# Revit family: Flushometer-Toilet_Touchless-KOHLER-Mach_Wave-K-40TD00N10_1
name_source: partatom
category: Plumbing Fixtures
units: mm (PartAtom-declared; Revit-internal decimal feet)

## family parameters
Cut with Voids When Loaded = No
Host = Face
OmniClass Number = 23.27.31.00
OmniClass Title = Valves
Part Type = Normal
Room Calculation Point = No
Round Connector Dimension = Use Diameter
Shared = No

## types (2) — shared parameters
ADA Compliant = Yes
Assembly Code = D2020
CW Connection = Yes
Center Distance = 11 5/8"
Cold Water Inlet = Cold Water Inlet
Cold Water Outlet = Cold Water Outlet
Date Modified = 12/27/2022
Default Elevation = 15"
Finish = Kohler-Metal-CP-Polished_Chrome
Flow Rate = 25 GPM
Flush Rate- GPF = 1.28 GPF
Flush Rate- LPF = 4.85 LPF
HW Connection = No
Hot Water Inlet = Hot Water Inlet
Length Of Retrofit Flush Valve = 2 1/2"
Manufacturer = Kohler Co.
Master Format 2014 = 23 09 13.33
Master Format 2014 Name = Flushometers
Material = Premium Metal Construction
Pressure = 80.00 psi
Product Documentation Link = https://www.us.kohler.com
Product Name = Mach Wave
Product Page URL = http://www.us.kohler.com
URL = https://www.us.kohler.com
Vent Connection = No
Waste Connection = No
Waste Water Outlet = Waste Water Outlet
Width Of Retrofit Flush Valve = 3 1/2"

## per-type parameters (varying)
| type | Description | Distance | Model | Retrofit Flush Valve | Toilet Flush Valve | Type | Vertical Distance For Connector | WaterSense Certified |
| Retrofit Flush Valve, CP-Polished Chrome | DC 1.28 gpf toilet flushometer retrofit | 0" | K-40TD00N10-RF-CP | Yes | No | 1 | 8 1/16" | No |
| Toilet Flush Valve, CP-Polished Chrome | DC 1.28 gpf toilet flushometer | 8 7/8" | K-40TD00N10-CP | No | Yes | 2 | 16 7/8" | Yes |

## geometry (parser evidence)
native form markers: Sweep x6
no freeform markers — native parametric forms only
